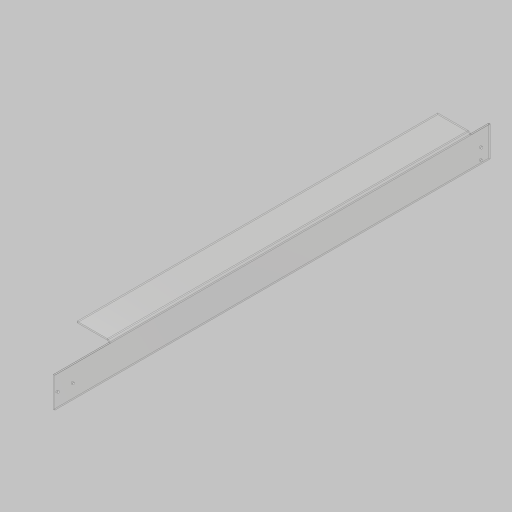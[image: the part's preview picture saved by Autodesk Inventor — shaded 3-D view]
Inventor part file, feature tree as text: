
AUTODESK INVENTOR PART (.ipt)
format: ipt  version: 2023.5 (Build 275446000, 446)  size: 157,184 bytes
history: native  units: in
note: dims shown in document units (in); Inventor stores cm internally (conversion verified against a paired STEP export)
features: sketch x6, sheet_metal_op x5, hole x2, other x2, projected_geometry x1
ambient origin geometry x8: Origin, YZ Plane, XZ Plane, XY Plane, X Axis, Y Axis, Z Axis, Center Point
bodies: Solid1 (feature_tree)
feature tree (16):
  sheet_metal_op  "Face1"
  hole  "Hole1"  [1 undecoded]
  hole  "Hole2"  [1 undecoded]
  sketch  "Sketch5"  dims[d6=0.201in d7=0.75in d8=0.385in d9=0.25in d10=0.5635in d11=0.125in]
  sheet_metal_op  "Face2"
  sheet_metal_op  "Fold3"
  sheet_metal_op  "Fold1"
  sketch  "Sketch1"  dims[d0=2.75in d1=39.375in]
  other  "Plate1"
  sketch  "Sketch2"  dims[d2=0.125in d3=0.3125in]
  sketch  "Sketch3"  dims[d4=1.375in]
  sketch  "Sketch4"  dims[d5=1.5in]
  other  "Plate2"
  sheet_metal_op  "Bend1"
  sketch  "Sketch6"  dims[d12=0.8108in d13=7.5in d14=0.125in d15=0.0625in d16=0.25in d17=0.125in d18=90.0deg d19=0.125in d20=1.0in d21=0.75in d22=0.201in d23=0.38in d24=0.385in d25=0.25in d26=0.5635in d27=0.125in d28=0.8108in d29=1.75in d30=5.0in d31=3.0in d32=0.125in d33=0.125in d34=0.0625in d35=0.25in d36=0.125in d43=0.125in d44=0.125in d45=0.0625in d46=0.25in d47=0.125in d48=90.0deg d49=0.125in d50=1.5in]
  projected_geometry  "Project Cut Edges1"
note: 2 required parameter values undecoded (feature->parameter linkage not recoverable at this tier; creation-order binding heuristic only, values carry confidence <= 0.55)
